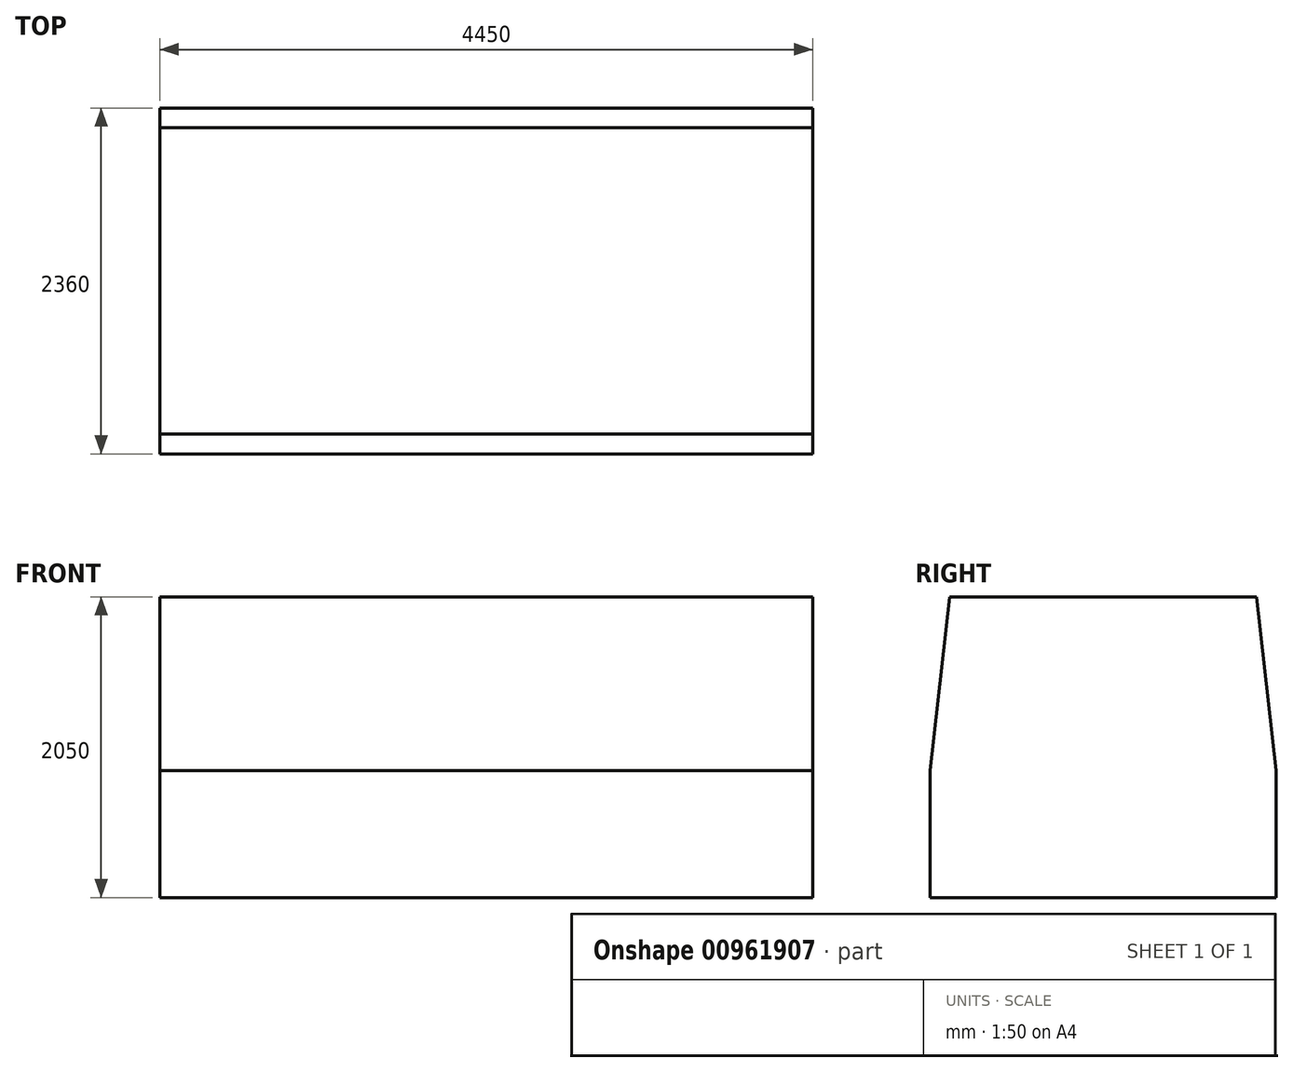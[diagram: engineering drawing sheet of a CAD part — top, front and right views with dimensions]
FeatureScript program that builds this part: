
annotation { "Feature Type Name" : "Feature", "Feature Type Description" : "" }
export const myFeature = defineFeature(function(context is Context, id is Id, definition is map)
    precondition{}
    {
        {
            var Q0;
            Q0=qCreatedBy(makeId("Right.planeOp"),FACE);
            var sketch = newSketch(context, id + "F0", { "sketchPlane" : qUnion([Q0])});
            skLineSegment(sketch, "E0", {"start": v(0, 0) * mm, "end": v(2360, 0) * mm});
            skLineSegment(sketch, "E1", {"start": v(0, 0) * mm, "end": v(0, 865) * mm});
            skLineSegment(sketch, "E2", {"start": v(2360, 0) * mm, "end": v(2360, 865) * mm});
            skLineSegment(sketch, "E3", {"start": v(0, 865) * mm, "end": v(135.01, 2050) * mm});
            skLineSegment(sketch, "E4", {"start": v(0, 865) * mm, "end": v(2360, 865) * mm, "construction": true});
            skLineSegment(sketch, "E5", {"start": v(2360, 865) * mm, "end": v(2224.99, 2050) * mm});
            skLineSegment(sketch, "E6", {"start": v(2224.99, 2050) * mm, "end": v(135.01, 2050) * mm});
            skSolve(sketch);
        }
        {
            var Q0;
            Q0=makeQuery(id+"F0.imprint","IMPRINT",FACE,{"disambiguationData":[TD([[makeQuery(id+"F0.imprint","IMPRINT",EDGE,{"derivedFrom":sQuery(id+"F0.wireOp",EDGE,"E0")}),1.0]])]});
            extrude(context, id + "F1", {"entities" : qUnion([Q0]), "flatOperationType" : FlatOperationType.REMOVE, "depth" : 4450 * mm, "offsetDistance" : 25 * mm, "domain" : OperationDomain.MODEL});
        }
    });
